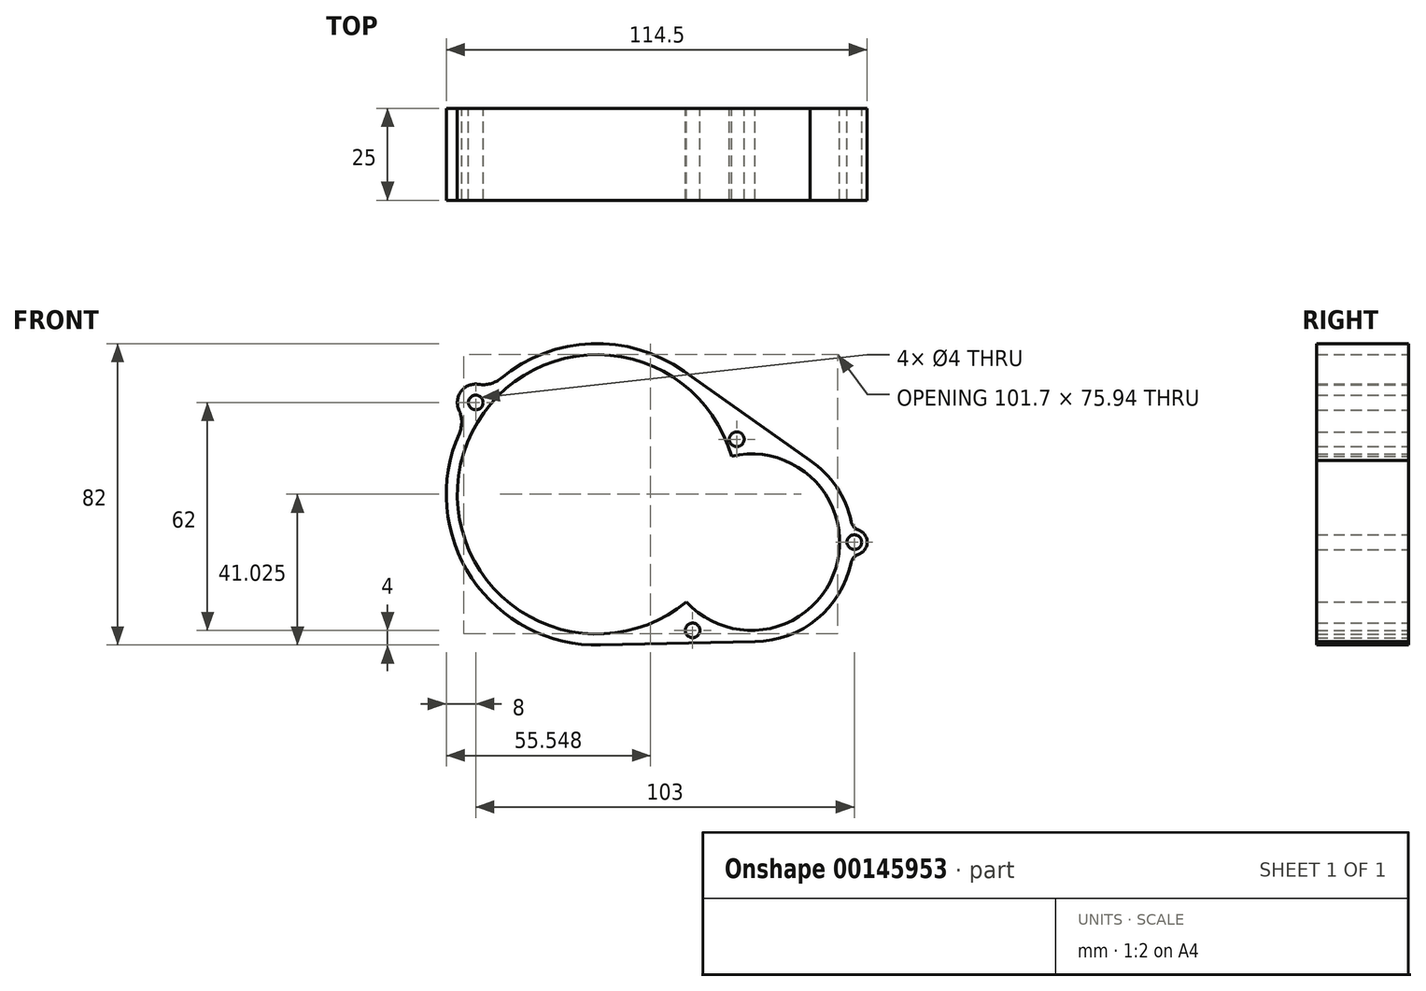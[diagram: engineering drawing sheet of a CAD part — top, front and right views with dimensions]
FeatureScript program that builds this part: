
annotation { "Feature Type Name" : "Feature", "Feature Type Description" : "" }
export const myFeature = defineFeature(function(context is Context, id is Id, definition is map)
    precondition{}
    {
        {
            var Q0;
            Q0=qCreatedBy(makeId("Front.planeOp"),FACE);
            var sketch = newSketch(context, id + "F0", { "sketchPlane" : qUnion([Q0])});
            skArc(sketch, "E0", {"start": v(36.56, 10.37) * mm, "mid": v(-36.3, 11.24) * mm, "end": v(24.3, -29.21) * mm});
            skArc(sketch, "E1", {"start": v(24.3, -29.21) * mm, "mid": v(64.93, -20.1) * mm, "end": v(36.56, 10.37) * mm});
            skCircle(sketch, "E2", {"center": v(-33, 25) * mm, "radius": 2 * mm});
            skCircle(sketch, "E3", {"center": v(38, 15) * mm, "radius": 2 * mm});
            skCircle(sketch, "E4", {"center": v(26, -37) * mm, "radius": 2 * mm});
            skCircle(sketch, "E5", {"center": v(70, -13) * mm, "radius": 2 * mm});
            skArc(sketch, "E6", {"start": v(23.64, 33.5) * mm, "mid": v(-1.6, 40.97) * mm, "end": v(-26.17, 31.56) * mm});
            skLineSegment(sketch, "E7", {"start": v(23.64, 33.5) * mm, "end": v(57.96, 9.28) * mm});
            skLineSegment(sketch, "E8", {"start": v(0.97, -40.99) * mm, "end": v(42.95, -40) * mm});
            skArc(sketch, "E9.trimOffspring", {"start": v(-37.47, 16.65) * mm, "mid": v(-34.11, -22.74) * mm, "end": v(0.97, -40.99) * mm});
            skArc(sketch, "E10", {"start": v(-32.18, 29.93) * mm, "mid": v(-36.99, 28.02) * mm, "end": v(-37.53, 22.88) * mm});
            skArc(sketch, "E11", {"start": v(-32.18, 29.93) * mm, "mid": v(-29, 30.1) * mm, "end": v(-26.17, 31.56) * mm});
            skArc(sketch, "E12", {"start": v(-37.47, 16.65) * mm, "mid": v(-36.82, 19.77) * mm, "end": v(-37.53, 22.88) * mm});
            skArc(sketch, "E13.trimOffspring", {"start": v(42.95, -40) * mm, "mid": v(59.82, -33.88) * mm, "end": v(69.13, -18.55) * mm});
            skArc(sketch, "E14", {"start": v(71.11, -16.32) * mm, "mid": v(73.5, -13) * mm, "end": v(71.11, -9.68) * mm});
            skArc(sketch, "E15.trimOffspring", {"start": v(69.13, -7.45) * mm, "mid": v(65.16, 2) * mm, "end": v(57.96, 9.28) * mm});
            skArc(sketch, "E16", {"start": v(69.13, -7.45) * mm, "mid": v(69.82, -8.83) * mm, "end": v(71.11, -9.68) * mm});
            skArc(sketch, "E17", {"start": v(71.11, -16.32) * mm, "mid": v(69.82, -17.17) * mm, "end": v(69.13, -18.55) * mm});
            skSolve(sketch);
        }
        {
            var Q0;
            Q0=makeQuery(id+"F0.imprint","IMPRINT",FACE,{"disambiguationData":[TD([[makeQuery(id+"F0.imprint","IMPRINT",EDGE,{"derivedFrom":sQuery(id+"F0.wireOp",EDGE,"E0")}),-1.0]])]});
            extrude(context, id + "F1", {"entities" : qUnion([Q0]), "depth" : 25 * mm});
        }
    });
